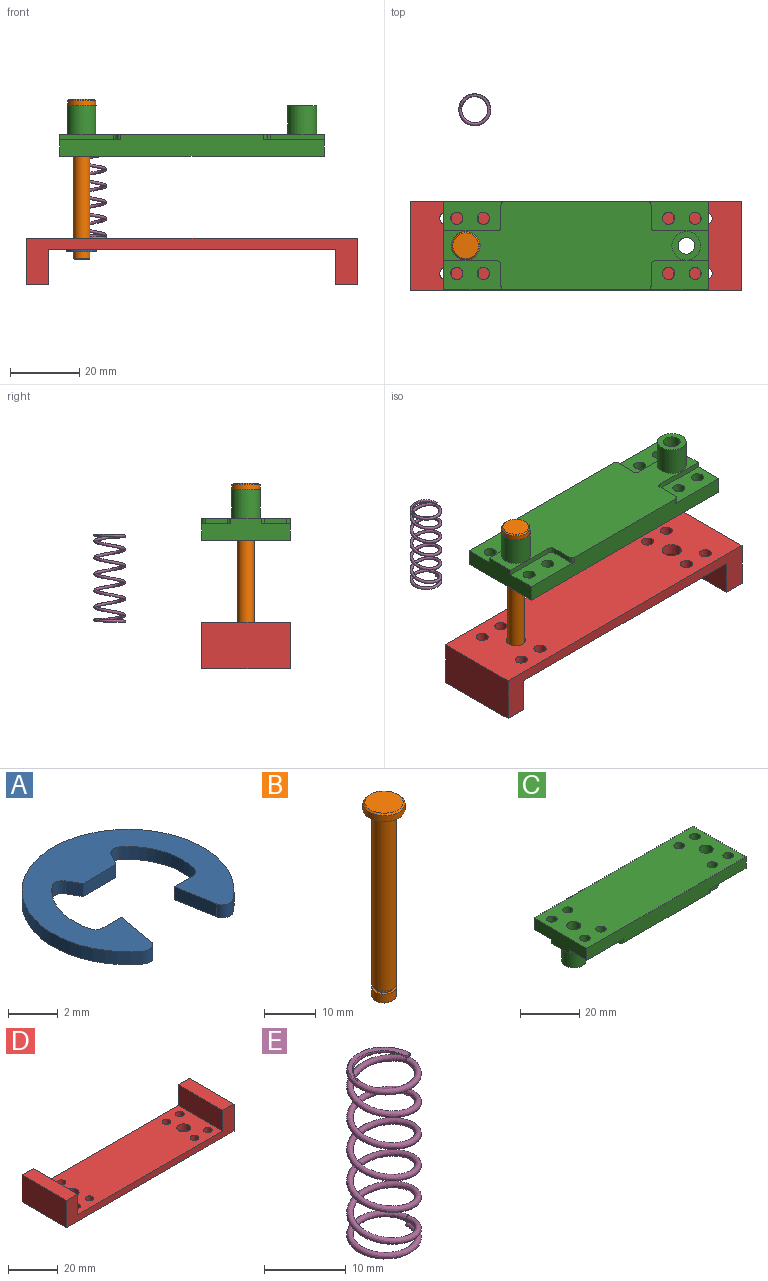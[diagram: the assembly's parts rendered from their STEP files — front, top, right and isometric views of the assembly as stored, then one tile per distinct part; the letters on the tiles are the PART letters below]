
ASSEMBLY  parts=5 mates=7
PART A: 18 faces, bbox 8.5x7.8x0.6 mm
  f0: plane 8.51x7.76mm, normal (0,0,1), area 28.3mm2, adj f2,f3,f4,f5,f6,f7,f8,f9
  f1: plane 8.51x7.76mm, normal (0,0,-1), area 28.3mm2, adj f2,f3,f4,f5,f6,f7,f8,f9
  f2: cylinder r=4.25mm len=8.51mm, axis (0,0,-1), area 13.5mm2, adj f0,f1,f16,f17
  f3: plane 2.04x0.64mm, normal (0.98,-0.17,0), area 1.3mm2, adj f0,f1,f6,f17
  f4: plane 0.64x0.64mm, normal (-0.87,-0.5,0), area 0.5mm2, adj f0,f1,f11,f14
  f5: cylinder r=3.06mm len=3.18mm, axis (0,0,1), area 2.2mm2, adj f0,f1,f14,f15
  f6: plane 1.05x0.64mm, normal (0,1,0), area 0.7mm2, adj f0,f1,f3,f15
  f7: cylinder r=3.06mm len=3.18mm, axis (0,0,1), area 2.2mm2, adj f0,f1,f12,f13
  f8: plane 1.05x0.64mm, normal (0,1,0), area 0.7mm2, adj f0,f1,f9,f12
  f9: plane 2.04x0.64mm, normal (-0.98,-0.17,0), area 1.3mm2, adj f0,f1,f8,f16
  f10: plane 0.64x0.64mm, normal (0.87,-0.5,0), area 0.5mm2, adj f0,f1,f11,f13
  f11: plane 1.87x0.64mm, normal (0,-1,0), area 1.2mm2, adj f0,f1,f4,f10
  f12: cylinder r=0.43mm len=0.64mm, axis (0,0,1), area 0.4mm2, adj f0,f1,f7,f8
  f13: cylinder r=0.43mm len=0.64mm, axis (0,0,1), area 0.5mm2, adj f0,f1,f7,f10
  f14: cylinder r=0.43mm len=0.64mm, axis (0,0,1), area 0.5mm2, adj f0,f1,f4,f5
  f15: cylinder r=0.43mm len=0.64mm, axis (0,0,1), area 0.4mm2, adj f0,f1,f5,f6
  f16: cylinder r=0.43mm len=0.67mm, axis (0,0,-1), area 0.5mm2, adj f0,f1,f2,f9
  f17: cylinder r=0.43mm len=0.67mm, axis (0,0,-1), area 0.5mm2, adj f0,f1,f2,f3
PART B: 11 faces, bbox 8.1x8.1x46.2 mm
  f0: cylinder r=2.38mm len=41.28mm, axis (0,0,-1), area 617.5mm2, adj f1,f6
  f1: plane 4.76x4.76mm, normal (0,0,-1), area 6.9mm2, adj f0,f2
  f2: cylinder r=1.87mm len=3.73mm, axis (0,0,1), area 8.6mm2, adj f1,f3
  f3: plane 4.76x4.76mm, normal (0,0,1), area 6.9mm2, adj f2,f5
  f4: plane 3.81x3.81mm, normal (0,0,-1), area 11.4mm2, adj f10
  f5: cylinder r=2.38mm len=4.76mm, axis (0,0,-1), area 29.4mm2, adj f3,f10
  f6: plane 8.13x8.13mm, normal (0,0,-1), area 34.1mm2, adj f0,f7
  f7: cylinder r=4.06mm len=8.13mm, axis (0,0,-1), area 36.3mm2, adj f6,f9
  f8: plane 7.42x7.42mm, normal (0,0,1), area 43.2mm2, adj f9
  f9: cone r=3.71mm half-angle=45deg, axis (0,0,-1), area 12.3mm2, adj f7,f8
  f10: cone r=2.38mm half-angle=45deg, axis (0,0,1), area 9.1mm2, adj f4,f5
PART C: 40 faces, bbox 76.2x25.4x14.6 mm
  f0: plane 76.2x6.35mm, normal (0,1,0), area 428.3mm2, adj f3,f6,f11,f13,f25,f29,f32,f36
  f1: cylinder r=1.75mm len=4.76mm, axis (0,0,-1), area 52.4mm2, adj f13,f29
  f2: cylinder r=1.75mm len=4.76mm, axis (0,0,-1), area 52.4mm2, adj f13,f29
  f3: plane 76.2x25.4mm, normal (0,0,-1), area 1276.2mm2, adj f0,f6,f11,f12,f16,f18,f21,f22
  f4: cylinder r=1.75mm len=4.76mm, axis (0,0,-1), area 52.4mm2, adj f13,f28
  f5: cylinder r=1.75mm len=4.76mm, axis (0,0,-1), area 52.4mm2, adj f13,f28
  f6: plane 25.4x6.35mm, normal (1,0,0), area 134.7mm2, adj f0,f3,f12,f13,f20,f21,f23,f25
  f7: cylinder r=1.75mm len=4.76mm, axis (0,0,-1), area 52.4mm2, adj f13,f25
  f8: cylinder r=1.75mm len=4.76mm, axis (0,0,-1), area 52.4mm2, adj f13,f25
  f9: cylinder r=1.75mm len=4.76mm, axis (0,0,-1), area 52.4mm2, adj f13,f20
  f10: cylinder r=1.75mm len=4.76mm, axis (0,0,-1), area 52.4mm2, adj f13,f20
  f11: plane 25.4x6.35mm, normal (-1,0,0), area 134.7mm2, adj f0,f3,f12,f13,f26,f28,f29,f30
  f12: plane 76.2x6.35mm, normal (0,-1,0), area 428.3mm2, adj f3,f6,f11,f13,f20,f28,f34,f38
  f13: plane 76.2x25.4mm, normal (0,0,1), area 1822.9mm2, adj f0,f1,f2,f4,f5,f6,f7,f8
  f14: cylinder r=2.38mm len=14.61mm, axis (0,0,1), area 218.5mm2, adj f13,f19
  f15: cylinder r=2.38mm len=14.61mm, axis (0,0,1), area 218.5mm2, adj f13,f17
  f16: cylinder r=4.13mm len=8.26mm, axis (0,0,1), area 214.1mm2, adj f3,f17
  f17: plane 8.26x8.26mm, normal (0,0,-1), area 35.7mm2, adj f15,f16
  f18: cylinder r=4.13mm len=8.26mm, axis (0,0,1), area 214.1mm2, adj f3,f19
  f19: plane 8.26x8.26mm, normal (0,0,-1), area 35.7mm2, adj f14,f18
  f20: plane 17.51x8.36mm, normal (0,0,-1), area 118.8mm2, adj f6,f9,f10,f12,f21,f22,f38,f39
  f21: plane 15.51x1.59mm, normal (0,-1,0), area 24.6mm2, adj f3,f6,f20,f39
  f22: plane 6.36x1.59mm, normal (1,0,0), area 10.1mm2, adj f3,f20,f38,f39
  f23: plane 15.51x1.59mm, normal (0,1,0), area 24.6mm2, adj f3,f6,f25,f37
  f24: plane 6.36x1.59mm, normal (1,0,0), area 10.1mm2, adj f3,f25,f36,f37
  f25: plane 17.51x8.36mm, normal (0,0,-1), area 118.8mm2, adj f0,f6,f7,f8,f23,f24,f36,f37
  f26: plane 15.51x1.59mm, normal (0,-1,0), area 24.6mm2, adj f3,f11,f28,f35
  f27: plane 6.36x1.59mm, normal (-1,0,0), area 10.1mm2, adj f3,f28,f34,f35
  f28: plane 17.51x8.36mm, normal (0,0,-1), area 118.8mm2, adj f4,f5,f11,f12,f26,f27,f34,f35
  f29: plane 17.51x8.36mm, normal (0,0,-1), area 118.8mm2, adj f0,f1,f2,f11,f30,f31,f32,f33
  f30: plane 15.51x1.59mm, normal (0,1,0), area 24.6mm2, adj f3,f11,f29,f33
  f31: plane 6.36x1.59mm, normal (-1,0,0), area 10.1mm2, adj f3,f29,f32,f33
  f32: cylinder r=1mm len=1.59mm, axis (0,0,-1), area 2.5mm2, adj f0,f3,f29,f31
  f33: cylinder r=1mm len=1.59mm, axis (0,0,1), area 2.5mm2, adj f3,f29,f30,f31
  f34: cylinder r=1mm len=1.59mm, axis (0,0,-1), area 2.5mm2, adj f3,f12,f27,f28
  f35: cylinder r=1mm len=1.59mm, axis (0,0,1), area 2.5mm2, adj f3,f26,f27,f28
  f36: cylinder r=1mm len=1.59mm, axis (0,0,1), area 2.5mm2, adj f0,f3,f24,f25
  f37: cylinder r=1mm len=1.59mm, axis (0,0,1), area 2.5mm2, adj f3,f23,f24,f25
  f38: cylinder r=1mm len=1.59mm, axis (0,0,1), area 2.5mm2, adj f3,f12,f20,f22
  f39: cylinder r=1mm len=1.59mm, axis (0,0,1), area 2.5mm2, adj f3,f20,f21,f22
PART D: 20 faces, bbox 95.3x25.4x13.3 mm
  f0: plane 82.55x25.4mm, normal (0,0,1), area 1971.9mm2, adj f1,f3,f6,f7,f8,f10,f12,f13
  f1: plane 95.25x13.34mm, normal (0,1,0), area 431.5mm2, adj f0,f2,f4,f5,f8,f9,f10,f11
  f2: plane 25.4x13.34mm, normal (-1,0,0), area 338.7mm2, adj f1,f3,f5,f9
  f3: plane 95.25x13.34mm, normal (0,-1,0), area 431.5mm2, adj f0,f2,f4,f5,f8,f9,f10,f11
  f4: plane 25.4x13.34mm, normal (1,0,0), area 338.7mm2, adj f1,f3,f5,f11
  f5: plane 95.25x25.4mm, normal (0,0,-1), area 2294.4mm2, adj f1,f2,f3,f4,f6,f7,f12,f13
  f6: cylinder r=2.76mm len=5.52mm, axis (0,0,1), area 55.1mm2, adj f0,f5
  f7: cylinder r=2.76mm len=5.52mm, axis (0,0,1), area 55.1mm2, adj f0,f5
  f8: plane 25.4x10.16mm, normal (1,0,0), area 258.1mm2, adj f0,f1,f3,f9
  f9: plane 25.4x6.35mm, normal (0,0,1), area 161.3mm2, adj f1,f2,f3,f8
  f10: plane 25.4x10.16mm, normal (-1,0,0), area 258.1mm2, adj f0,f1,f3,f11
  f11: plane 25.4x6.35mm, normal (0,0,1), area 161.3mm2, adj f1,f3,f4,f10
  f12: cylinder r=1.75mm len=3.5mm, axis (0,0,-1), area 34.9mm2, adj f0,f5
  f13: cylinder r=1.75mm len=3.5mm, axis (0,0,-1), area 34.9mm2, adj f0,f5
  f14: cylinder r=1.75mm len=3.5mm, axis (0,0,-1), area 34.9mm2, adj f0,f5
  f15: cylinder r=1.75mm len=3.5mm, axis (0,0,-1), area 34.9mm2, adj f0,f5
  f16: cylinder r=1.75mm len=3.5mm, axis (0,0,-1), area 34.9mm2, adj f0,f5
  f17: cylinder r=1.75mm len=3.5mm, axis (0,0,-1), area 34.9mm2, adj f0,f5
  f18: cylinder r=1.75mm len=3.5mm, axis (0,0,-1), area 34.9mm2, adj f0,f5
  f19: cylinder r=1.75mm len=3.5mm, axis (0,0,-1), area 34.9mm2, adj f0,f5
PART E: 8 faces, bbox 9.5x9.1x26.2 mm
  f0: bspline ~9.14x9.13mm, area 56.8mm2, adj f1,f2,f3,f7
  f1: bspline ~2.51x1.47mm, area 0mm2, adj f0,f7
  f2: plane 0.81x0.41mm, normal (0,-1,0), area 0.3mm2, adj f0,f7
  f3: bspline ~24.53x9.14mm, area 340mm2, adj f0,f5
  f4: plane 0.81x0.41mm, normal (0,1,-0.03), area 0.3mm2, adj f5,f6
  f5: bspline ~9.14x9.13mm, area 56.5mm2, adj f3,f4,f6
  f6: plane 8.77x4.52mm, normal (0,0,-1), area 8.1mm2, adj f4,f5
  f7: plane 8.77x4.52mm, normal (0,0,1), area 6.9mm2, adj f0,f1,f2
PLACE A rot(axis=(0,0,-1),180deg) t=(-31.75,0,-14.02)mm
PLACE B rot(axis=(0,0,-1),180deg) t=(-31.75,0,-13.97)mm
PLACE C rot(axis=(1,0,0),180deg) t=(0,0,0)mm fixed
PLACE D rot(axis=(-1,0,0),180deg) t=(0,0,20.85)mm
PLACE E rot(axis=(-0.04,-1,0.06),0deg) t=(-29.15,39.22,-4.55)mm
MATE cylindrical B.f0 <-> C.f16  axis (0,0,-1) through (-31.75,0,-12.38)mm
MATE planar C.f16 <-> B.f0  axis (0,0,1) through (-31.75,0,8.25)mm
MATE planar A.f0 <-> D.f0  axis (0,0,1) through (-31.75,-0.76,-33.12)mm
MATE cylindrical B.f0 <-> D.f7  axis (0,0,-1) through (-31.75,0,-12.38)mm
MATE planar E.f6 <-> D.f5  axis (0,0,-1) through (-28.27,36.39,-29.95)mm
MATE revolute A.f2 <-> B.f0  axis (0,0,-1) through (-31.75,0,-33.76)mm
MATE cylindrical D.f6 <-> C.f18  axis (0,0,-1) through (31.75,0,-29.95)mm
